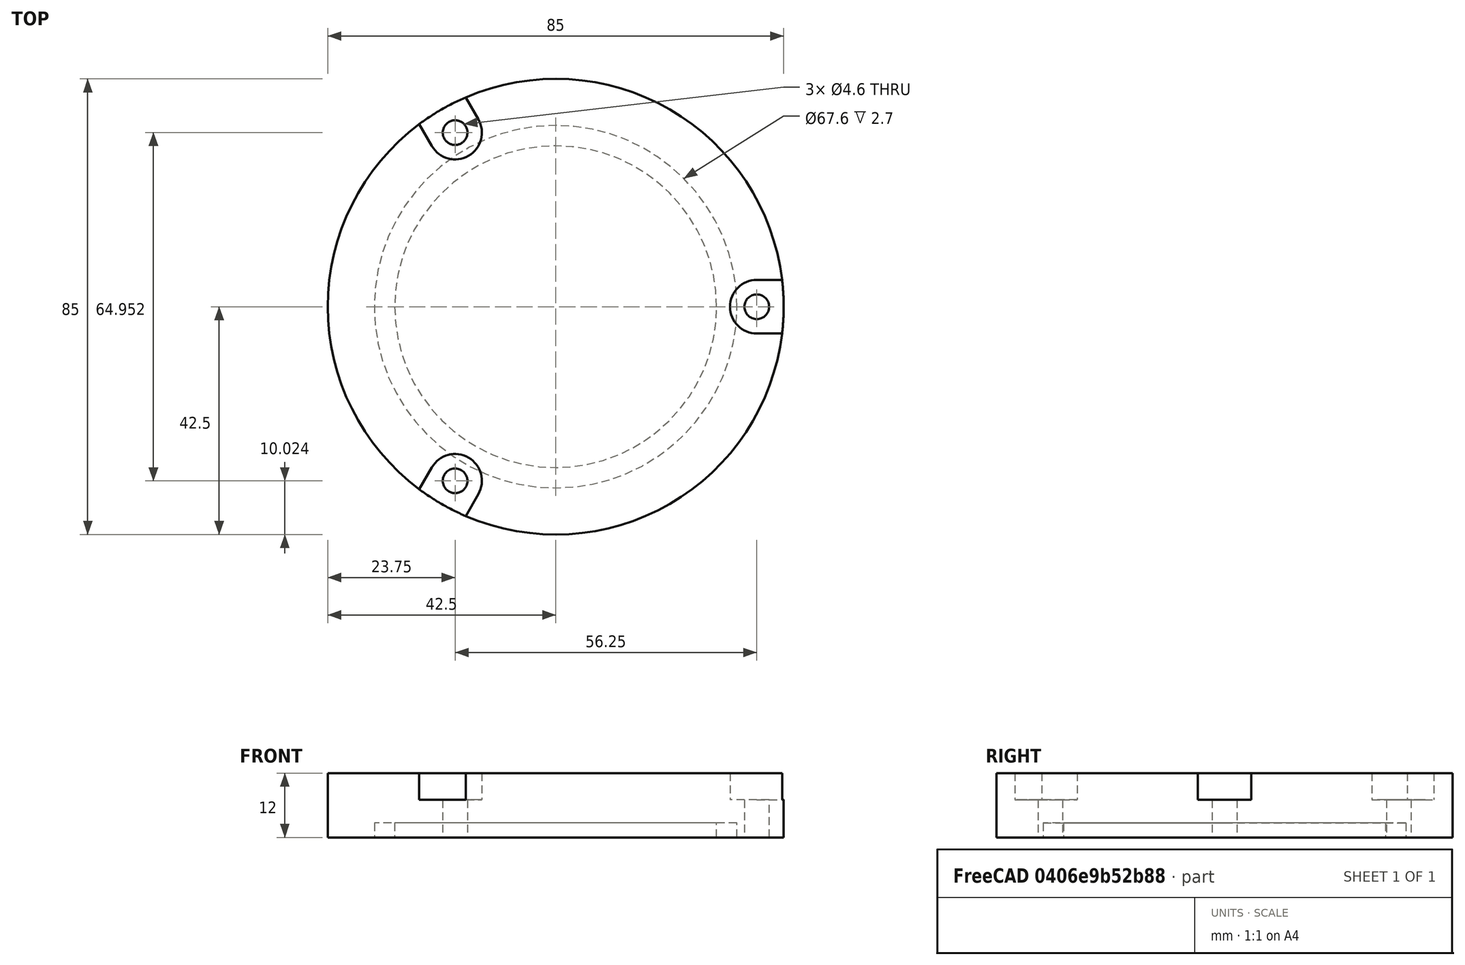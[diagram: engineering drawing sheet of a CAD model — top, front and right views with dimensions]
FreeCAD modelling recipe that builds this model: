
FCSTD DOCUMENT  (FreeCAD 0.20R29603 (Git))
Label: PhilippsXL30_Blindflange
License: All rights reserved
LicenseURL: http://en.wikipedia.org/wiki/All_rights_reserved
objects: TechDraw::DrawViewDimension×18, Part::Cylinder×9, Part::MultiFuse×4, TechDraw::DrawProjGroupItem×4, Part::Box×3, Part::Cut×2, TechDraw::DrawSVGTemplate×2, TechDraw::DrawProjGroup×2, TechDraw::DrawPage×2, Part::Compound×1, Part::Feature×1, TechDraw::DrawViewSection×1
note: 20 computed .brp shape members not serialized (recipe doc carries the construction recipe); baked Part::Feature solids carry a one-line shape summary decoded from their .brp

FEATURE [Part::Cylinder] Cylinder  label="Zylinder"
  Angle = 360
  AttacherType = Attacher::AttachEngine3D
  FirstAngle = 0
  Height = 12
  Radius = 42.5
  SecondAngle = 0
FEATURE [Part::Cylinder] Cylinder001  label="Zylinder001"
  Angle = 360
  AttacherType = Attacher::AttachEngine3D
  FirstAngle = 0
  Height = 2.7
  Radius = 33.8
  SecondAngle = 0
FEATURE [Part::Cut] Cut
  Base = -> Cylinder
  Tool = -> Cylinder001
FEATURE [Part::Cylinder] Cylinder002  label="Zylinder002"
  Angle = 360
  AttacherType = Attacher::AttachEngine3D
  FirstAngle = 0
  Height = 2.7
  Radius = 30
  SecondAngle = 0
FEATURE [Part::MultiFuse] Fusion
  Shapes = -> [Cylinder002,Cut]
FEATURE [Part::Cylinder] Cylinder003  label="Zylinder003"
  Angle = 360
  AttacherType = Attacher::AttachEngine3D
  FirstAngle = 0
  Height = 12
  Placement = pos=(37.5,0,0) rot=(0,0,1;0rad)
  Radius = 2.3
  SecondAngle = 0
FEATURE [Part::Cylinder] Cylinder004  label="Zylinder004"
  Angle = 360
  AttacherType = Attacher::AttachEngine3D
  FirstAngle = 0
  Height = 5
  Placement = pos=(37.5,0,7) rot=(0,0,1;0rad)
  Radius = 5
  SecondAngle = 0
FEATURE [Part::Box] Box  label="Würfel"
  AttacherType = Attacher::AttachEngine3D
  Height = 5
  Length = 10
  Placement = pos=(37.5,-5,7) rot=(0,0,1;0rad)
  Width = 10
FEATURE [Part::MultiFuse] Fusion001
  Shapes = -> [Box,Cylinder003,Cylinder004]
FEATURE [Part::Box] Box001  label="Würfel001"
  AttacherType = Attacher::AttachEngine3D
  Height = 5
  Length = 10
  Placement = pos=(37.5,-5,7) rot=(0,0,1;0rad)
  Width = 10
FEATURE [Part::Cylinder] Cylinder005  label="Zylinder005"
  Angle = 360
  AttacherType = Attacher::AttachEngine3D
  FirstAngle = 0
  Height = 12
  Placement = pos=(37.5,0,0) rot=(0,0,1;0rad)
  Radius = 2.3
  SecondAngle = 0
FEATURE [Part::Cylinder] Cylinder006  label="Zylinder006"
  Angle = 360
  AttacherType = Attacher::AttachEngine3D
  FirstAngle = 0
  Height = 5
  Placement = pos=(37.5,0,7) rot=(0,0,1;0rad)
  Radius = 5
  SecondAngle = 0
FEATURE [Part::MultiFuse] Fusion002
  Placement = pos=(0,0,0) rot=(0,0,1;2.0944rad)
  Shapes = -> [Box001,Cylinder005,Cylinder006]
FEATURE [Part::Box] Box002  label="Würfel002"
  AttacherType = Attacher::AttachEngine3D
  Height = 5
  Length = 10
  Placement = pos=(37.5,-5,7) rot=(0,0,1;0rad)
  Width = 10
FEATURE [Part::Cylinder] Cylinder007  label="Zylinder007"
  Angle = 360
  AttacherType = Attacher::AttachEngine3D
  FirstAngle = 0
  Height = 12
  Placement = pos=(37.5,0,0) rot=(0,0,1;0rad)
  Radius = 2.3
  SecondAngle = 0
FEATURE [Part::Cylinder] Cylinder008  label="Zylinder008"
  Angle = 360
  AttacherType = Attacher::AttachEngine3D
  FirstAngle = 0
  Height = 5
  Placement = pos=(37.5,0,7) rot=(0,0,1;0rad)
  Radius = 5
  SecondAngle = 0
FEATURE [Part::MultiFuse] Fusion003
  Placement = pos=(0,0,0) rot=(0,0,1;4.18879rad)
  Shapes = -> [Box002,Cylinder007,Cylinder008]
FEATURE [Part::Compound] Compound
  Links = -> [Fusion001,Fusion002,Fusion003]
FEATURE [Part::Cut] Cut001
  Base = -> Fusion
  Tool = -> Compound
FEATURE [Part::Feature] Cut001_solid  label="Cut001 (Solid)"
  shape: bbox 85 x 85 x 12 mm, 31 faces (baked)
FEATURE [TechDraw::DrawSVGTemplate] Template
  EditableTexts = Designed_by_Name=Thomas Spielauer; FC-Date=2023-06-20; FC-SC=mm; FC-SH=01/02; FC-Title=Philipps XL30 compatible; Subtitle=Blind flange
  Height = 210
  Orientation = 1
  Width = 297
FEATURE [TechDraw::DrawProjGroupItem] ProjItem  label="Front"
  CoarseView = false
  Direction = (0,0,1)
  Focus = 100
  HardHidden = false
  IsoCount = 0
  IsoHidden = false
  IsoVisible = false
  LockPosition = true
  Perspective = false
  Rotation = 0
  RotationVector = (1,0,0)
  ScaleType = 2
  SeamHidden = false
  SeamVisible = true
  SmoothHidden = false
  SmoothVisible = true
  Source = -> [Cut001]
  Type = 0
  X = 0
  XDirection = (1,0,0)
  Y = 0
FEATURE [TechDraw::DrawProjGroupItem] ProjItem001  label="Left"
  CoarseView = false
  Direction = (-1,0,1e-16)
  Focus = 100
  HardHidden = false
  IsoCount = 0
  IsoHidden = false
  IsoVisible = false
  LockPosition = false
  Perspective = false
  Rotation = 0
  RotationVector = (1,0,0)
  ScaleType = 2
  SeamHidden = false
  SeamVisible = true
  SmoothHidden = false
  SmoothVisible = true
  Source = -> [Cut001]
  Type = 1
  X = 85
  XDirection = (1e-16,0,1)
  Y = 0
FEATURE [TechDraw::DrawProjGroupItem] ProjItem002  label="Rear"
  CoarseView = false
  Direction = (0,0,-1)
  Focus = 100
  HardHidden = false
  IsoCount = 0
  IsoHidden = false
  IsoVisible = false
  LockPosition = false
  Perspective = false
  Rotation = 0
  RotationVector = (1,0,0)
  ScaleType = 2
  SeamHidden = false
  SeamVisible = true
  SmoothHidden = false
  SmoothVisible = true
  Source = -> [Cut001]
  Type = 3
  X = 170
  XDirection = (-1,0,0)
  Y = 0
FEATURE [TechDraw::DrawProjGroup] ProjGroup
  Anchor = -> ProjItem
  AutoDistribute = true
  LockPosition = false
  ProjectionType = 0
  Rotation = 0
  ScaleType = 0
  Source = -> [Cut001]
  Views = -> [ProjItem,ProjItem001,ProjItem002]
  X = 62.2182
  Y = 138.514
  spacingX = 0
  spacingY = 15
FEATURE [TechDraw::DrawViewDimension] Dimension
  AngleOverride = false
  Arbitrary = false
  ArbitraryTolerances = false
  EqualTolerance = true
  ExtensionAngle = 0
  FormatSpec = ⌀%.2w
  FormatSpecOverTolerance = %+.2w
  FormatSpecUnderTolerance = %+.2w
  Inverted = false
  LineAngle = 0
  LockPosition = false
  MeasureType = 1
  OverTolerance = 0
  References2D = -> [ProjItem]
  Rotation = 0
  ScaleType = 0
  TheoreticalExact = false
  Type = 5
  UnderTolerance = 0
  X = 42.3439
  Y = 32.9337
FEATURE [TechDraw::DrawViewDimension] Dimension001
  AngleOverride = false
  Arbitrary = false
  ArbitraryTolerances = false
  EqualTolerance = true
  ExtensionAngle = 0
  FormatSpec = %.2w
  FormatSpecOverTolerance = %+.2w
  FormatSpecUnderTolerance = %+.2w
  Inverted = false
  LineAngle = 0
  LockPosition = false
  MeasureType = 1
  OverTolerance = 0
  References2D = -> [ProjItem]
  Rotation = 0
  ScaleType = 0
  TheoreticalExact = false
  Type = 0
  UnderTolerance = 0
  X = 53.0814
  Y = 14.1282
FEATURE [TechDraw::DrawViewDimension] Dimension002
  AngleOverride = false
  Arbitrary = false
  ArbitraryTolerances = false
  EqualTolerance = true
  ExtensionAngle = 0
  FormatSpec = ⌀%.2w
  FormatSpecOverTolerance = %+.2w
  FormatSpecUnderTolerance = %+.2w
  Inverted = false
  LineAngle = 0
  LockPosition = false
  MeasureType = 1
  OverTolerance = 0
  References2D = -> [ProjItem]
  Rotation = 0
  ScaleType = 0
  TheoreticalExact = false
  Type = 5
  UnderTolerance = 0
  X = -30.7018
  Y = 44.8387
FEATURE [TechDraw::DrawViewDimension] Dimension003
  AngleOverride = false
  Arbitrary = false
  ArbitraryTolerances = false
  EqualTolerance = true
  ExtensionAngle = 0
  FormatSpec = %.2w
  FormatSpecOverTolerance = %+.2w
  FormatSpecUnderTolerance = %+.2w
  Inverted = false
  LineAngle = 0
  LockPosition = false
  MeasureType = 1
  OverTolerance = 0
  References2D = -> [ProjItem001]
  Rotation = 0
  ScaleType = 0
  TheoreticalExact = false
  Type = 0
  UnderTolerance = 0
  X = -13.9258
  Y = 53.86
FEATURE [TechDraw::DrawViewDimension] Dimension004
  AngleOverride = false
  Arbitrary = false
  ArbitraryTolerances = false
  EqualTolerance = true
  ExtensionAngle = 0
  FormatSpec = ⌀%.2w
  FormatSpecOverTolerance = %+.2w
  FormatSpecUnderTolerance = %+.2w
  Inverted = false
  LineAngle = 0
  LockPosition = false
  MeasureType = 1
  OverTolerance = 0
  References2D = -> [ProjItem002]
  Rotation = 0
  ScaleType = 0
  TheoreticalExact = false
  Type = 5
  UnderTolerance = 0
  X = -60.8736
  Y = 12.5448
FEATURE [TechDraw::DrawViewDimension] Dimension005
  AngleOverride = false
  Arbitrary = false
  ArbitraryTolerances = false
  EqualTolerance = true
  ExtensionAngle = 0
  FormatSpec = %.2w
  FormatSpecOverTolerance = %+.2w
  FormatSpecUnderTolerance = %+.2w
  Inverted = false
  LineAngle = 0
  LockPosition = false
  MeasureType = 1
  OverTolerance = 0
  References2D = -> [ProjItem002]
  Rotation = 0
  ScaleType = 0
  TheoreticalExact = false
  Type = 0
  UnderTolerance = 0
  X = -52.547
  Y = -5.94991
FEATURE [TechDraw::DrawViewDimension] Dimension006
  AngleOverride = false
  Arbitrary = false
  ArbitraryTolerances = false
  EqualTolerance = true
  ExtensionAngle = 0
  FormatSpec = ⌀%.2w
  FormatSpecOverTolerance = %+.2w
  FormatSpecUnderTolerance = %+.2w
  Inverted = false
  LineAngle = 0
  LockPosition = false
  MeasureType = 1
  OverTolerance = 0
  References2D = -> [ProjItem002]
  Rotation = 0
  ScaleType = 0
  TheoreticalExact = false
  Type = 5
  UnderTolerance = 0
  X = -57.9142
  Y = 19.6484
FEATURE [TechDraw::DrawViewDimension] Dimension007
  AngleOverride = false
  Arbitrary = false
  ArbitraryTolerances = false
  EqualTolerance = true
  ExtensionAngle = 0
  FormatSpec = %.2w
  FormatSpecOverTolerance = %+.2w
  FormatSpecUnderTolerance = %+.2w
  Inverted = false
  LineAngle = 0
  LockPosition = false
  MeasureType = 1
  OverTolerance = 0
  References2D = -> [ProjItem002]
  Rotation = 0
  ScaleType = 0
  TheoreticalExact = false
  Type = 6
  UnderTolerance = 0
  X = 16.4121
  Y = 53.4955
FEATURE [TechDraw::DrawViewDimension] Dimension008
  AngleOverride = false
  Arbitrary = false
  ArbitraryTolerances = false
  EqualTolerance = true
  ExtensionAngle = 0
  FormatSpec = ⌀%.2w
  FormatSpecOverTolerance = %+.2w
  FormatSpecUnderTolerance = %+.2w
  Inverted = false
  LineAngle = 0
  LockPosition = false
  MeasureType = 1
  OverTolerance = 0
  References2D = -> [ProjItem002]
  Rotation = 0
  ScaleType = 0
  TheoreticalExact = false
  Type = 5
  UnderTolerance = 0
  X = -2.66999
  Y = 15.5066
FEATURE [TechDraw::DrawPage] Page
  KeepUpdated = true
  NextBalloonIndex = 1
  ProjectionType = 0
  Template = -> Template
  Views = -> [ProjGroup,Dimension,Dimension001,Dimension002,Dimension003,Dimension004,Dimension005,Dimension006,Dimension007,Dimension008]
FEATURE [TechDraw::DrawSVGTemplate] Template001
  EditableTexts = Designed_by_Name=Thomas Spielauer; FC-Date=2023-06-20; FC-SC=mm; FC-SH=02/02; FC-Title=Philipps XL30 compatible; Subtitle=Blind flange
  Height = 210
  Orientation = 1
  Width = 297
FEATURE [TechDraw::DrawProjGroupItem] ProjItem003  label="Front001"
  CoarseView = false
  Direction = (0,0,1)
  Focus = 100
  HardHidden = false
  IsoCount = 0
  IsoHidden = false
  IsoVisible = false
  LockPosition = true
  Perspective = false
  Rotation = 0
  RotationVector = (1,0,0)
  ScaleType = 2
  SeamHidden = false
  SeamVisible = true
  SmoothHidden = false
  SmoothVisible = true
  Source = -> [Cut001]
  Type = 0
  X = 0
  XDirection = (-2e-16,1,0)
  Y = 0
FEATURE [TechDraw::DrawProjGroup] ProjGroup001
  Anchor = -> ProjItem003
  AutoDistribute = true
  LockPosition = false
  ProjectionType = 0
  Rotation = 0
  ScaleType = 0
  Source = -> [Cut001]
  Views = -> [ProjItem003]
  X = 75.4641
  Y = 137.417
  spacingX = 15
  spacingY = 15
FEATURE [TechDraw::DrawViewSection] SectionView  label="Section  - "
  BaseView = -> ProjItem003
  CoarseView = false
  CutSurfaceDisplay = 2
  Direction = (2e-16,-1,0)
  FileGeomPattern = <path>
  FileHatchPattern = <path>
  Focus = 100
  FuseBeforeCut = false
  HardHidden = false
  HatchScale = 1
  IsoCount = 0
  IsoHidden = false
  IsoVisible = false
  LockPosition = false
  NameGeomPattern = Diamond
  Perspective = false
  Rotation = 0
  Scale = 1.3
  ScaleType = 2
  SeamHidden = false
  SeamVisible = true
  SectionDirection = 0
  SectionNormal = (2e-16,-1,0)
  SectionOrigin = (0,0,6)
  SmoothHidden = false
  SmoothVisible = true
  Source = -> [Cut001]
  X = 184.042
  XDirection = (0,0,1)
  Y = 133.121
FEATURE [TechDraw::DrawViewDimension] Dimension009
  AngleOverride = false
  Arbitrary = false
  ArbitraryTolerances = false
  EqualTolerance = true
  ExtensionAngle = 0
  FormatSpec = %.2w
  FormatSpecOverTolerance = %+.2w
  FormatSpecUnderTolerance = %+.2w
  Inverted = false
  LineAngle = 0
  LockPosition = false
  MeasureType = 1
  OverTolerance = 0
  References2D = -> [SectionView]
  Rotation = 0
  ScaleType = 0
  TheoreticalExact = false
  Type = 0
  UnderTolerance = 0
  X = -23.2852
  Y = 38.4899
FEATURE [TechDraw::DrawViewDimension] Dimension010
  AngleOverride = false
  Arbitrary = false
  ArbitraryTolerances = false
  EqualTolerance = true
  ExtensionAngle = 0
  FormatSpec = %.2w
  FormatSpecOverTolerance = %+.2w
  FormatSpecUnderTolerance = %+.2w
  Inverted = false
  LineAngle = 0
  LockPosition = false
  MeasureType = 1
  OverTolerance = 0
  References2D = -> [SectionView]
  Rotation = 0
  ScaleType = 0
  TheoreticalExact = false
  Type = 0
  UnderTolerance = 0
  X = -24.8123
  Y = 66.041
FEATURE [TechDraw::DrawViewDimension] Dimension011
  AngleOverride = false
  Arbitrary = false
  ArbitraryTolerances = false
  EqualTolerance = true
  ExtensionAngle = 0
  FormatSpec = %.2w
  FormatSpecOverTolerance = %+.2w
  FormatSpecUnderTolerance = %+.2w
  Inverted = false
  LineAngle = 0
  LockPosition = false
  MeasureType = 1
  OverTolerance = 0
  References2D = -> [SectionView]
  Rotation = 0
  ScaleType = 0
  TheoreticalExact = false
  Type = 0
  UnderTolerance = 0
  X = -20.0035
  Y = -30.1281
FEATURE [TechDraw::DrawViewDimension] Dimension012
  AngleOverride = false
  Arbitrary = false
  ArbitraryTolerances = false
  EqualTolerance = true
  ExtensionAngle = 0
  FormatSpec = %.2w
  FormatSpecOverTolerance = %+.2w
  FormatSpecUnderTolerance = %+.2w
  Inverted = false
  LineAngle = 0
  LockPosition = false
  MeasureType = 1
  OverTolerance = 0
  References2D = -> [SectionView]
  Rotation = 0
  ScaleType = 0
  TheoreticalExact = false
  Type = 0
  UnderTolerance = 0
  X = -19.4124
  Y = -58.8844
FEATURE [TechDraw::DrawViewDimension] Dimension013
  AngleOverride = false
  Arbitrary = false
  ArbitraryTolerances = false
  EqualTolerance = true
  ExtensionAngle = 0
  FormatSpec = %.2w
  FormatSpecOverTolerance = %+.2w
  FormatSpecUnderTolerance = %+.2w
  Inverted = false
  LineAngle = 0
  LockPosition = false
  MeasureType = 1
  OverTolerance = 0
  References2D = -> [SectionView]
  Rotation = 0
  ScaleType = 0
  TheoreticalExact = false
  Type = 0
  UnderTolerance = 0
  X = 24.0198
  Y = -45.0891
FEATURE [TechDraw::DrawViewDimension] Dimension014
  AngleOverride = false
  Arbitrary = false
  ArbitraryTolerances = false
  EqualTolerance = true
  ExtensionAngle = 0
  FormatSpec = %.2w
  FormatSpecOverTolerance = %+.2w
  FormatSpecUnderTolerance = %+.2w
  Inverted = false
  LineAngle = 0
  LockPosition = false
  MeasureType = 1
  OverTolerance = 0
  References2D = -> [SectionView]
  Rotation = 0
  ScaleType = 0
  TheoreticalExact = false
  Type = 0
  UnderTolerance = 0
  X = -37.656
  Y = 51.6763
FEATURE [TechDraw::DrawViewDimension] Dimension015
  AngleOverride = false
  Arbitrary = false
  ArbitraryTolerances = false
  EqualTolerance = true
  ExtensionAngle = 0
  FormatSpec = %.2w
  FormatSpecOverTolerance = %+.2w
  FormatSpecUnderTolerance = %+.2w
  Inverted = false
  LineAngle = 0
  LockPosition = false
  MeasureType = 1
  OverTolerance = 0
  References2D = -> [SectionView]
  Rotation = 0
  ScaleType = 0
  TheoreticalExact = false
  Type = 0
  UnderTolerance = 0
  X = -28.7079
  Y = 44.1633
FEATURE [TechDraw::DrawViewDimension] Dimension016
  AngleOverride = false
  Arbitrary = false
  ArbitraryTolerances = false
  EqualTolerance = true
  ExtensionAngle = 0
  FormatSpec = ⌀%.2w
  FormatSpecOverTolerance = %+.2w
  FormatSpecUnderTolerance = %+.2w
  Inverted = false
  LineAngle = 0
  LockPosition = false
  MeasureType = 1
  OverTolerance = 0
  References2D = -> [ProjItem003]
  Rotation = 0
  ScaleType = 0
  TheoreticalExact = false
  Type = 5
  UnderTolerance = 0
  X = 16.805
  Y = 11.0537
FEATURE [TechDraw::DrawViewDimension] Dimension017
  AngleOverride = false
  Arbitrary = false
  ArbitraryTolerances = false
  EqualTolerance = true
  ExtensionAngle = 0
  FormatSpec = ⌀%.2w
  FormatSpecOverTolerance = %+.2w
  FormatSpecUnderTolerance = %+.2w
  Inverted = false
  LineAngle = 0
  LockPosition = false
  MeasureType = 1
  OverTolerance = 0
  References2D = -> [ProjItem003]
  Rotation = 0
  ScaleType = 0
  TheoreticalExact = false
  Type = 5
  UnderTolerance = 0
  X = 19.1547
  Y = 30.2309
FEATURE [TechDraw::DrawPage] Page001
  KeepUpdated = true
  NextBalloonIndex = 1
  ProjectionType = 0
  Template = -> Template001
  Views = -> [ProjGroup001,SectionView,Dimension009,Dimension010,Dimension011,Dimension012,Dimension013,Dimension014,Dimension015,Dimension016,Dimension017]
note: 2 file-system paths scrubbed to <path> (originals preserved in the JSON sidecar)
